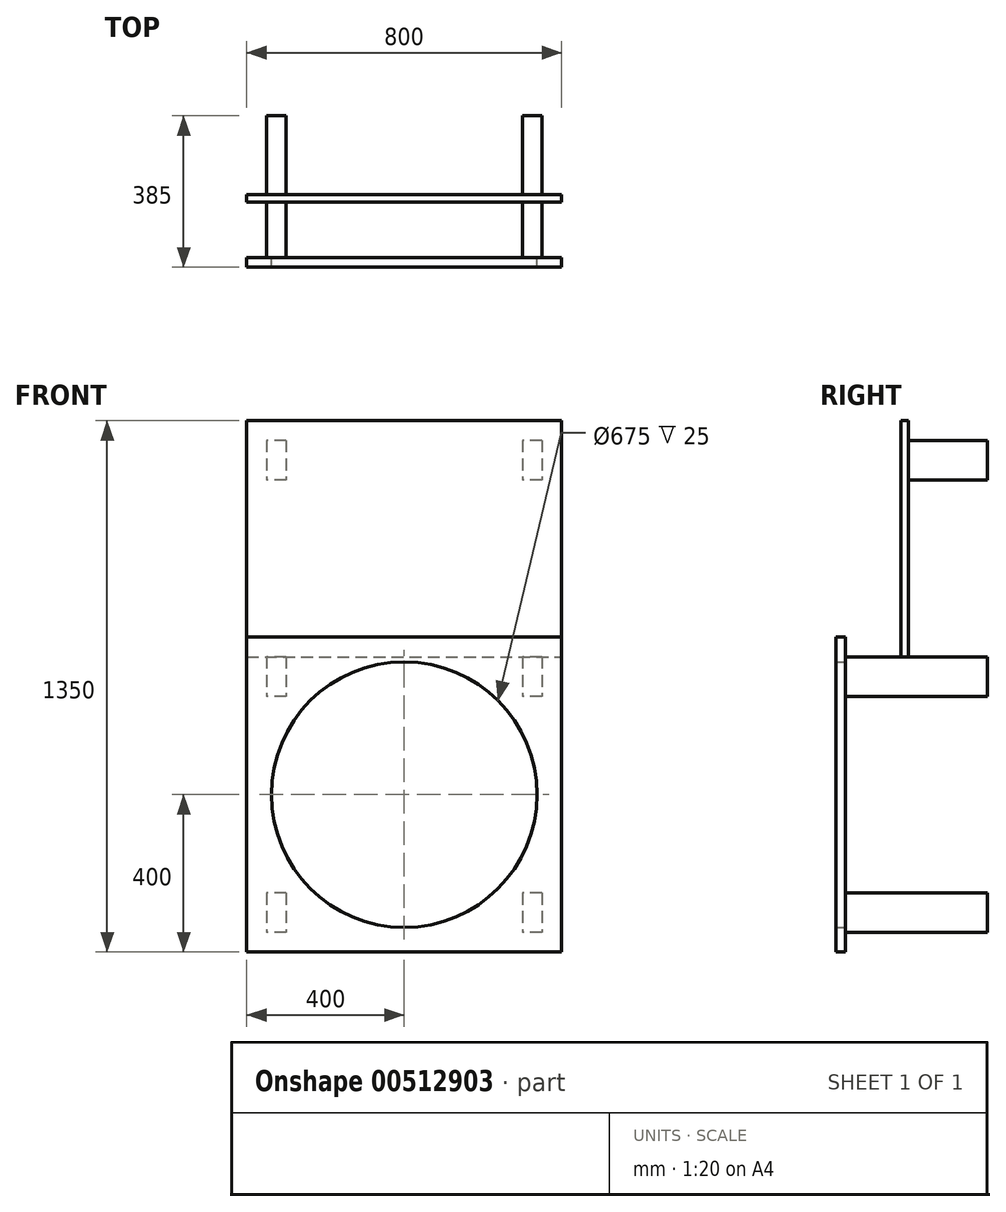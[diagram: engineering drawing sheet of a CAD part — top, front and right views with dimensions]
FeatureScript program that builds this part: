
annotation { "Feature Type Name" : "Feature", "Feature Type Description" : "" }
export const myFeature = defineFeature(function(context is Context, id is Id, definition is map)
    precondition{}
    {
        {
            var Q0;
            Q0=qCreatedBy(makeId("Front.planeOp"),FACE);
            var sketch = newSketch(context, id + "F0", { "sketchPlane" : qUnion([Q0])});
            skLineSegment(sketch, "E0.bottom", {"start": v(0, 0) * mm, "end": v(800, 0) * mm});
            skLineSegment(sketch, "E0.top", {"start": v(0, -800) * mm, "end": v(800, -800) * mm});
            skLineSegment(sketch, "E0.left", {"start": v(0, 0) * mm, "end": v(0, -800) * mm});
            skLineSegment(sketch, "E0.right", {"start": v(800, 0) * mm, "end": v(800, -800) * mm});
            skCircle(sketch, "E1", {"center": v(400, -400) * mm, "radius": 337.5 * mm});
            skSolve(sketch);
        }
        {
            var Q0;
            Q0=makeQuery(id+"F0.imprint","IMPRINT",FACE,{"disambiguationData":[TD([[makeQuery(id+"F0.imprint","IMPRINT",EDGE,{"derivedFrom":sQuery(id+"F0.wireOp",EDGE,"E0.bottom")}),-1.0]])]});
            extrude(context, id + "F1", {"entities" : qUnion([Q0]), "depth" : 25 * mm});
        }
        {
            var Q0;
            Q0=makeQuery(id+"F1.opExtrude","CAP_FACE",FACE,{"disambiguationData":[OSD([sQuery(id+"F0.wireOp",EDGE,"E0.bottom"),sQuery(id+"F0.wireOp",EDGE,"E0.top"),sQuery(id+"F0.wireOp",EDGE,"E0.left"),sQuery(id+"F0.wireOp",EDGE,"E0.right"),sQuery(id+"F0.wireOp",EDGE,"E1")])],"isStart":true});
            var sketch = newSketch(context, id + "F2", { "sketchPlane" : qUnion([Q0])});
            skLineSegment(sketch, "E2.bottom", {"start": v(-750, -50) * mm, "end": v(-700, -50) * mm});
            skLineSegment(sketch, "E2.top", {"start": v(-750, -150) * mm, "end": v(-700, -150) * mm});
            skLineSegment(sketch, "E2.left", {"start": v(-750, -50) * mm, "end": v(-750, -150) * mm});
            skLineSegment(sketch, "E2.right", {"start": v(-700, -50) * mm, "end": v(-700, -150) * mm});
            skLineSegment(sketch, "E3.0.1.0", {"start": v(-700, -650) * mm, "end": v(-700, -750) * mm});
            skLineSegment(sketch, "E3.0.1.1", {"start": v(-750, -650) * mm, "end": v(-700, -650) * mm});
            skLineSegment(sketch, "E3.0.1.2", {"start": v(-750, -650) * mm, "end": v(-750, -750) * mm});
            skLineSegment(sketch, "E3.0.1.3", {"start": v(-750, -750) * mm, "end": v(-700, -750) * mm});
            skLineSegment(sketch, "E3.1.0.0", {"start": v(-50, -50) * mm, "end": v(-50, -150) * mm});
            skLineSegment(sketch, "E3.1.0.1", {"start": v(-100, -50) * mm, "end": v(-50, -50) * mm});
            skLineSegment(sketch, "E3.1.0.2", {"start": v(-100, -50) * mm, "end": v(-100, -150) * mm});
            skLineSegment(sketch, "E3.1.0.3", {"start": v(-100, -150) * mm, "end": v(-50, -150) * mm});
            skLineSegment(sketch, "E3.1.1.0", {"start": v(-50, -650) * mm, "end": v(-50, -750) * mm});
            skLineSegment(sketch, "E3.1.1.1", {"start": v(-100, -650) * mm, "end": v(-50, -650) * mm});
            skLineSegment(sketch, "E3.1.1.2", {"start": v(-100, -650) * mm, "end": v(-100, -750) * mm});
            skLineSegment(sketch, "E3.1.1.3", {"start": v(-100, -750) * mm, "end": v(-50, -750) * mm});
            skLineSegment(sketch, "E3.direction1", {"start": v(-750, -150) * mm, "end": v(-100, -150) * mm, "construction": true});
            skLineSegment(sketch, "E3.direction2", {"start": v(-750, -150) * mm, "end": v(-750, -750) * mm, "construction": true});
            skSolve(sketch);
        }
        {
            var Q0;
            Q0 = qSketchRegion(id + "F2", true);
            extrude(context, id + "F3", {"entities" : qUnion([Q0]), "operationType" : NewBodyOperationType.ADD, "depth" : 360 * mm});
        }
        {
            var Q0;
            Q0=makeQuery(id+"F3.opExtrude","CAP_FACE",FACE,{"disambiguationData":[OSD([sQuery(id+"F2.wireOp",EDGE,"E3.1.0.0"),sQuery(id+"F2.wireOp",EDGE,"E3.1.0.1"),sQuery(id+"F2.wireOp",EDGE,"E3.1.0.2"),sQuery(id+"F2.wireOp",EDGE,"E3.1.0.3")])],"isStart":false});
            var sketch = newSketch(context, id + "F4", { "sketchPlane" : qUnion([Q0])});
            skLineSegment(sketch, "E4.bottom", {"start": v(0, -50) * mm, "end": v(-800, -50) * mm});
            skLineSegment(sketch, "E4.top", {"start": v(0, 550) * mm, "end": v(-800, 550) * mm});
            skLineSegment(sketch, "E4.left", {"start": v(0, -50) * mm, "end": v(0, 550) * mm});
            skLineSegment(sketch, "E4.right", {"start": v(-800, -50) * mm, "end": v(-800, 550) * mm});
            skLineSegment(sketch, "E5.bottom", {"start": v(-100, 500) * mm, "end": v(-50, 500) * mm});
            skLineSegment(sketch, "E5.top", {"start": v(-100, 400) * mm, "end": v(-50, 400) * mm});
            skLineSegment(sketch, "E5.left", {"start": v(-100, 500) * mm, "end": v(-100, 400) * mm});
            skLineSegment(sketch, "E5.right", {"start": v(-50, 500) * mm, "end": v(-50, 400) * mm});
            skLineSegment(sketch, "E6.bottom", {"start": v(-750, 500) * mm, "end": v(-700, 500) * mm});
            skLineSegment(sketch, "E6.top", {"start": v(-750, 400) * mm, "end": v(-700, 400) * mm});
            skLineSegment(sketch, "E6.left", {"start": v(-750, 500) * mm, "end": v(-750, 400) * mm});
            skLineSegment(sketch, "E6.right", {"start": v(-700, 500) * mm, "end": v(-700, 400) * mm});
            skSolve(sketch);
        }
        {
            var Q0;
            Q0=makeQuery(id+"F4.imprint","IMPRINT",FACE,{"disambiguationData":[TD([[makeQuery(id+"F4.imprint","IMPRINT",EDGE,{"derivedFrom":sQuery(id+"F4.wireOp",EDGE,"E6.bottom")}),-1.0]])]});
            var Q1;
            Q1=makeQuery(id+"F4.imprint","IMPRINT",FACE,{"disambiguationData":[TD([[makeQuery(id+"F4.imprint","IMPRINT",EDGE,{"derivedFrom":sQuery(id+"F4.wireOp",EDGE,"E5.bottom")}),-1.0]])]});
            extrude(context, id + "F5", {"entities" : qUnion([Q0, Q1]), "oppositeDirection" : true, "depth" : 200 * mm, "offsetDistance" : 25 * mm});
        }
        {
            var Q0;
            Q0=makeQuery(id+"F5.opExtrude","CAP_FACE",FACE,{"disambiguationData":[OSD([sQuery(id+"F4.wireOp",EDGE,"E6.bottom"),sQuery(id+"F4.wireOp",EDGE,"E6.top"),sQuery(id+"F4.wireOp",EDGE,"E6.left"),sQuery(id+"F4.wireOp",EDGE,"E6.right")])],"isStart":false});
            var sketch = newSketch(context, id + "F6", { "sketchPlane" : qUnion([Q0])});
            skLineSegment(sketch, "E7.bottom", {"start": v(0, 550) * mm, "end": v(800, 550) * mm});
            skLineSegment(sketch, "E7.top", {"start": v(0, -50) * mm, "end": v(800, -50) * mm});
            skLineSegment(sketch, "E7.left", {"start": v(0, 550) * mm, "end": v(0, -50) * mm});
            skLineSegment(sketch, "E7.right", {"start": v(800, 550) * mm, "end": v(800, -50) * mm});
            skSolve(sketch);
        }
        {
            var Q0;
            Q0 = qSketchRegion(id + "F6", true);
            extrude(context, id + "F7", {"entities" : qUnion([Q0]), "depth" : 20 * mm, "offsetDistance" : 25 * mm});
        }
    });
